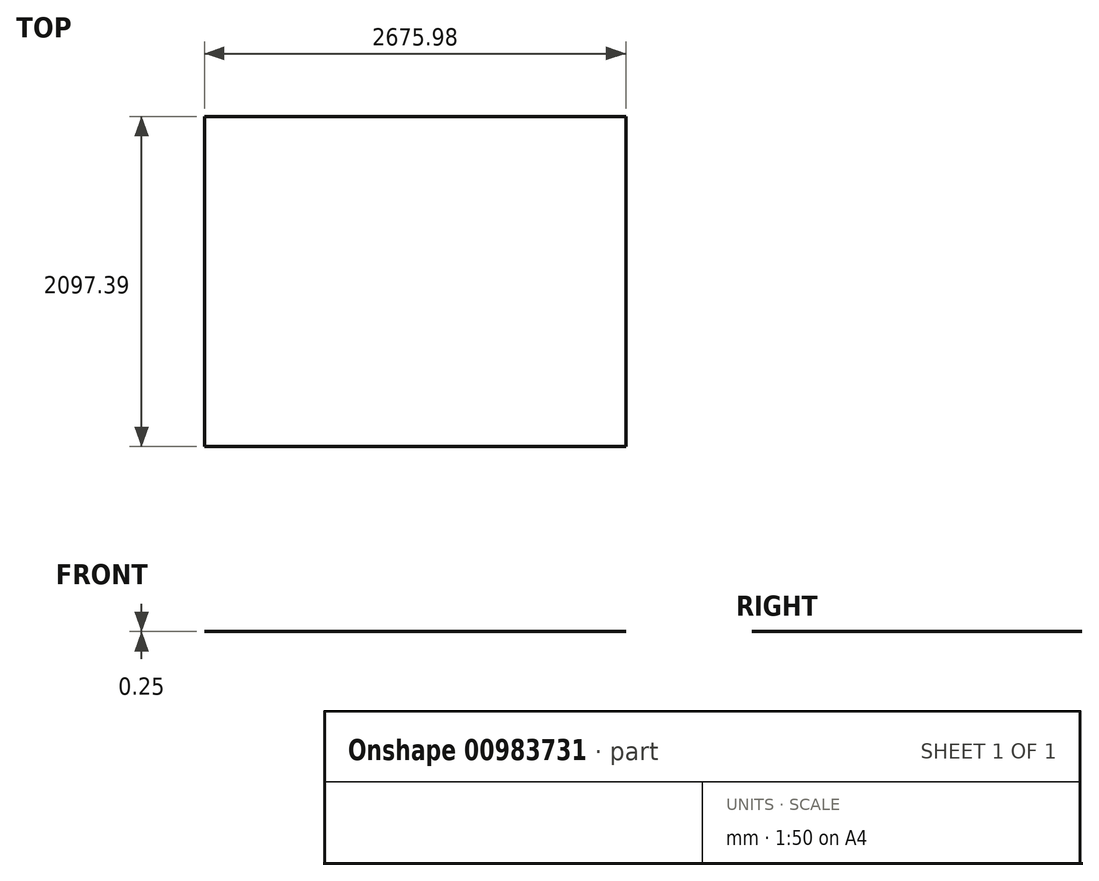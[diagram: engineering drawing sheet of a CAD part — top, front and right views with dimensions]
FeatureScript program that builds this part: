
annotation { "Feature Type Name" : "Feature", "Feature Type Description" : "" }
export const myFeature = defineFeature(function(context is Context, id is Id, definition is map)
    precondition{}
    {
        {
            var Q0;
            Q0=qCreatedBy(makeId("Top.planeOp"),FACE);
            var sketch = newSketch(context, id + "F0", { "sketchPlane" : qUnion([Q0])});
            skLineSegment(sketch, "E0.bottom", {"start": v(-4657.94, 3268.25) * mm, "end": v(-7333.92, 3268.25) * mm});
            skLineSegment(sketch, "E0.top", {"start": v(-4657.94, 5365.64) * mm, "end": v(-7333.92, 5365.64) * mm});
            skLineSegment(sketch, "E0.left", {"start": v(-4657.94, 3268.25) * mm, "end": v(-4657.94, 5365.64) * mm});
            skLineSegment(sketch, "E0.right", {"start": v(-7333.92, 3268.25) * mm, "end": v(-7333.92, 5365.64) * mm});
            skSolve(sketch);
        }
        {
            var Q0;
            Q0 = qSketchRegion(id + "F0", true);
            extrude(context, id + "F1", {"entities" : qUnion([Q0]), "depth" : 0.25 * mm, "offsetDistance" : 25.4 * mm});
        }
    });
